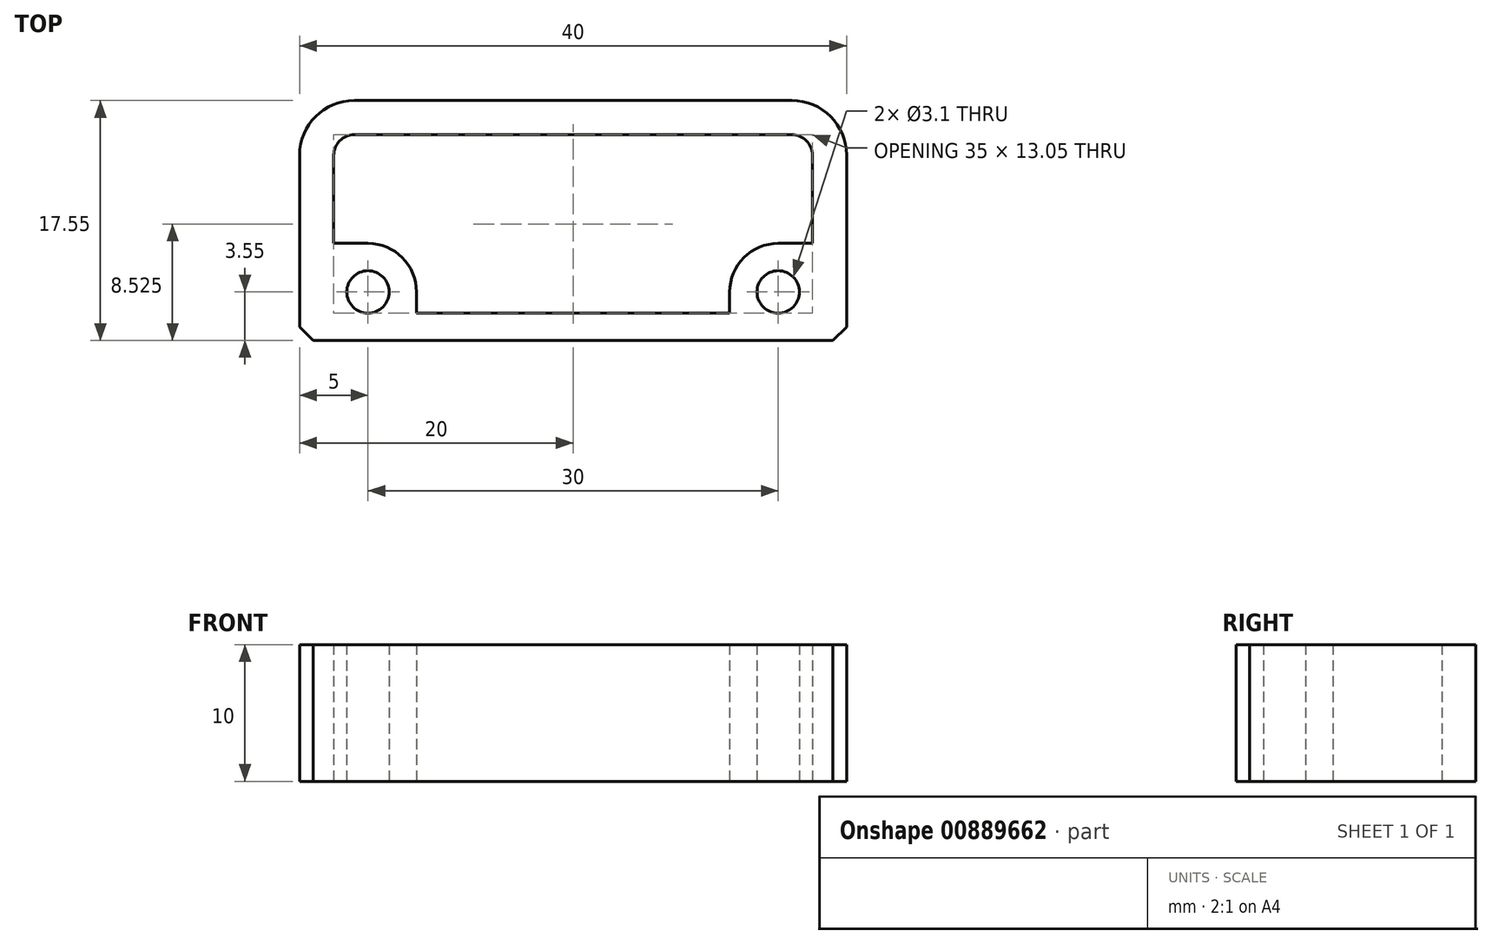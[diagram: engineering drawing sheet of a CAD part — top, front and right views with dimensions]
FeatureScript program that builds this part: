
annotation { "Feature Type Name" : "Feature", "Feature Type Description" : "" }
export const myFeature = defineFeature(function(context is Context, id is Id, definition is map)
    precondition{}
    {
        {
            var Q0;
            Q0=qCreatedBy(makeId("Top.planeOp"),FACE);
            var sketch = newSketch(context, id + "F0", { "sketchPlane" : qUnion([Q0])});
            skLineSegment(sketch, "E0", {"start": v(0, 0) * mm, "end": v(0, 29.32) * mm, "construction": true});
            skLineSegment(sketch, "E1", {"start": v(0, 0) * mm, "end": v(28.83, 0) * mm, "construction": true});
            skLineSegment(sketch, "E2", {"start": v(0, 17.55) * mm, "end": v(16, 17.55) * mm});
            skLineSegment(sketch, "E3", {"start": v(20, 13.55) * mm, "end": v(20, 0) * mm});
            skCircle(sketch, "E4", {"center": v(15, 3.55) * mm, "radius": 1.55 * mm});
            skPoint(sketch, "E5.visualSharp", {"position": v(20, 17.55) * mm});
            skArc(sketch, "E5.filletArc", {"start": v(20, 13.55) * mm, "mid": v(18.83, 16.38) * mm, "end": v(16, 17.55) * mm});
            skLineSegment(sketch, "E6.0", {"start": v(17.5, 13.55) * mm, "end": v(17.5, 7.1) * mm});
            skLineSegment(sketch, "E6.1", {"start": v(0, 15.05) * mm, "end": v(16, 15.05) * mm});
            skArc(sketch, "E7.0", {"start": v(17.5, 13.55) * mm, "mid": v(17.06, 14.61) * mm, "end": v(16, 15.05) * mm});
            skArc(sketch, "E8", {"start": v(15, 7.1) * mm, "mid": v(12.49, 6.06) * mm, "end": v(11.45, 3.55) * mm});
            skLineSegment(sketch, "E9", {"start": v(15, 7.1) * mm, "end": v(17.5, 7.1) * mm});
            skLineSegment(sketch, "E10", {"start": v(11.45, 3.55) * mm, "end": v(11.45, 2) * mm});
            skLineSegment(sketch, "E11", {"start": v(11.45, 2) * mm, "end": v(0, 2) * mm});
            skLineSegment(sketch, "E12", {"start": v(20, 0) * mm, "end": v(0, 0) * mm});
            skLineSegment(sketch, "E13", {"start": v(0, 17.55) * mm, "end": v(0, 15.05) * mm});
            skLineSegment(sketch, "E14", {"start": v(0, 0) * mm, "end": v(0, 2) * mm});
            skSolve(sketch);
        }
        {
            var Q0;
            Q0 = qSketchRegion(id + "F0", true);
            extrude(context, id + "F1", {"entities" : qUnion([Q0]), "depth" : 10 * mm, "offsetDistance" : 25 * mm});
        }
        {
            var Q0;
            Q0=makeQuery(id+"F1.opExtrude","SWEPT_BODY",BODY,{"disambiguationData":[OSD([sQuery(id+"F0.wireOp",EDGE,"E2"),sQuery(id+"F0.wireOp",EDGE,"E3"),sQuery(id+"F0.wireOp",EDGE,"E4"),sQuery(id+"F0.wireOp",EDGE,"E5.filletArc"),sQuery(id+"F0.wireOp",EDGE,"E6.0"),sQuery(id+"F0.wireOp",EDGE,"E6.1"),sQuery(id+"F0.wireOp",EDGE,"E7.0"),sQuery(id+"F0.wireOp",EDGE,"E8"),sQuery(id+"F0.wireOp",EDGE,"E9"),sQuery(id+"F0.wireOp",EDGE,"E10"),sQuery(id+"F0.wireOp",EDGE,"E11"),sQuery(id+"F0.wireOp",EDGE,"E12"),sQuery(id+"F0.wireOp",EDGE,"E13"),sQuery(id+"F0.wireOp",EDGE,"E14")])]});
            var Q1;
            Q1=makeQuery(id+"F1.opExtrude","SWEPT_FACE",FACE,{"disambiguationData":[OSD([sQuery(id+"F0.wireOp",EDGE,"E13")])]});
            mirror(context, id + "F2", {"operationType" : NewBodyOperationType.ADD, "entities" : qUnion([Q0]), "mirrorPlane" : qUnion([Q1])});
        }
        {
            var Q0;
            Q0=makeQuery(id+"F2.opPattern","COPY",EDGE,{"derivedFrom":makeQuery(id+"F1.opExtrude","SWEPT_EDGE",EDGE,{"disambiguationData":[OSD([sQuery(id+"F0.wireOp",EDGE,"E3"),sQuery(id+"F0.wireOp",EDGE,"E12")])]}),"instanceName":"1"});
            var Q1;
            Q1=makeQuery(id+"F1.opExtrude","SWEPT_EDGE",EDGE,{"disambiguationData":[OSD([sQuery(id+"F0.wireOp",EDGE,"E3"),sQuery(id+"F0.wireOp",EDGE,"E12")])]});
            chamfer(context, id + "F3", {"entities" : qUnion([Q0, Q1]), "width" : 1 * mm, "tangentPropagation" : true});
        }
    });
